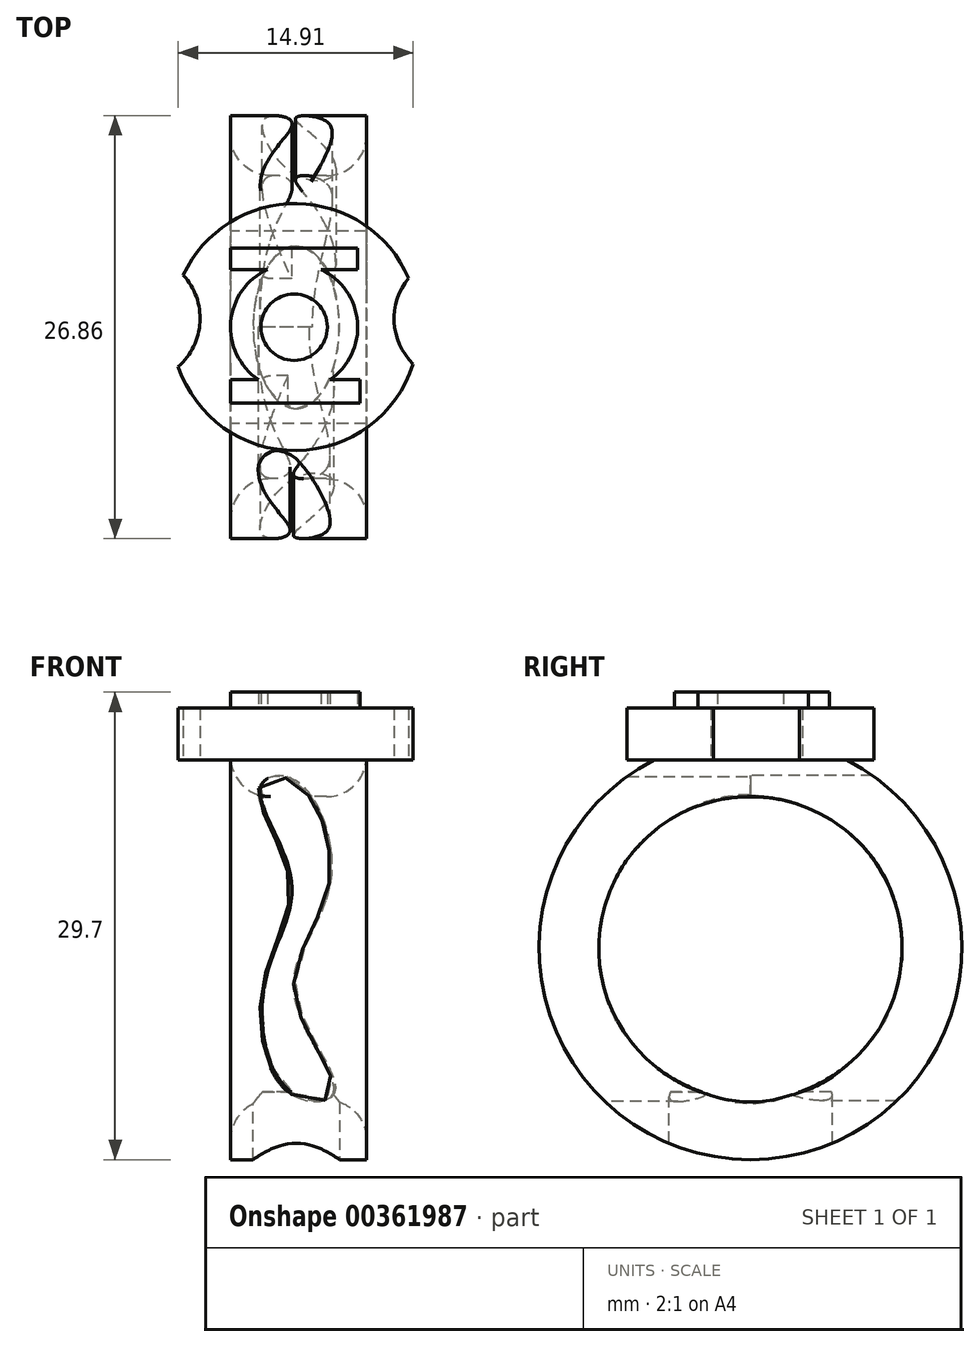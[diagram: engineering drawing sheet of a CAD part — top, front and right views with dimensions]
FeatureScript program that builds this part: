
annotation { "Feature Type Name" : "Feature", "Feature Type Description" : "" }
export const myFeature = defineFeature(function(context is Context, id is Id, definition is map)
    precondition{}
    {
        {
            var Q0;
            Q0=qCreatedBy(makeId("Right.planeOp"),FACE);
            var sketch = newSketch(context, id + "F0", { "sketchPlane" : qUnion([Q0])});
            skCircle(sketch, "E0", {"center": v(0, 9.13) * mm, "radius": 9.63 * mm});
            skCircle(sketch, "E1", {"center": v(0, 9.13) * mm, "radius": 13.43 * mm});
            skArc(sketch, "E2", {"start": v(-4.66, 21.72) * mm, "mid": v(0.04, 18.8) * mm, "end": v(4.75, 21.69) * mm});
            skArc(sketch, "E3", {"start": v(4.75, 21.69) * mm, "mid": v(0.06, 24.06) * mm, "end": v(-4.66, 21.72) * mm});
            skSolve(sketch);
        }
        {
            var Q0;
            Q0 = qSketchRegion(id + "F0", true);
            extrude(context, id + "F1", {"entities" : qUnion([Q0]), "depth" : 8.64 * mm});
        }
        {
            var Q0;
            Q0=makeQuery(id+"F1.opExtrude","CAP_EDGE",EDGE,{"disambiguationData":[OSD([sQuery(id+"F0.wireOp",EDGE,"E0")])],"isStart":false});
            var Q1;
            Q1=makeQuery(id+"F1.opExtrude","CAP_EDGE",EDGE,{"disambiguationData":[OSD([sQuery(id+"F0.wireOp",EDGE,"E0")])],"isStart":true});
            fillet(context, id + "F2", {"entities" : qUnion([Q0, Q1]), "radius" : 2.54 * mm, "tangentPropagation" : true, "allowEdgeOverflow" : false});
        }
        {
            var Q0;
            Q0=qCreatedBy(makeId("Top.planeOp"),FACE);
            cPlane(context, id + "F3", {"entities" : qUnion([Q0]), "cplaneType" : CPlaneType.OFFSET, "offset" : 8.9 * mm, "width" : 152.4 * mm, "height" : 152.4 * mm});
        }
        {
            var Q0;
            Q0=qCreatedBy(makeId("Right.planeOp"),FACE);
            var sketch = newSketch(context, id + "F4", { "sketchPlane" : qUnion([Q0])});
            skCircle(sketch, "E4", {"center": v(11.39, 21.41) * mm, "radius": 5.94 * mm});
            skSolve(sketch);
        }
        {
            var Q0;
            Q0 = qSketchRegion(id + "F4", true);
            extrude(context, id + "F5", {"entities" : qUnion([Q0]), "operationType" : NewBodyOperationType.REMOVE, "depth" : 27.94 * mm});
        }
        {
            var Q0;
            Q0=makeQuery(id+"F1.opExtrude","SWEPT_BODY",BODY,{"disambiguationData":[OSD([sQuery(id+"F0.wireOp",EDGE,"E0"),sQuery(id+"F0.wireOp",EDGE,"E1"),sQuery(id+"F0.wireOp",EDGE,"E3")])]});
            var Q1;
            Q1=qCreatedBy(makeId("Front.planeOp"),FACE);
            mirror(context, id + "F6", {"operationType" : NewBodyOperationType.ADD, "entities" : qUnion([Q0]), "mirrorPlane" : qUnion([Q1])});
        }
        {
            var Q0;
            Q0=qCreatedBy(id+"F3.planeOp",FACE);
            cPlane(context, id + "F7", {"entities" : qUnion([Q0]), "cplaneType" : CPlaneType.OFFSET, "offset" : 12.2 * mm, "width" : 152.4 * mm, "height" : 152.4 * mm});
        }
        {
            var Q0;
            Q0=qCreatedBy(id+"F7.planeOp",FACE);
            var sketch = newSketch(context, id + "F8", { "sketchPlane" : qUnion([Q0])});
            skCircle(sketch, "E5", {"center": v(4.1, 0) * mm, "radius": 7.84 * mm});
            skSolve(sketch);
        }
        {
            var Q0;
            Q0 = qSketchRegion(id + "F8", true);
            extrude(context, id + "F9", {"entities" : qUnion([Q0]), "operationType" : NewBodyOperationType.ADD, "depth" : 3.3 * mm});
        }
        {
            var Q0;
            Q0=qCreatedBy(id+"F7.planeOp",FACE);
            var sketch = newSketch(context, id + "F10", { "sketchPlane" : qUnion([Q0])});
            skLineSegment(sketch, "E6.bottom", {"start": v(0, 5) * mm, "end": v(8.08, 5) * mm});
            skLineSegment(sketch, "E6.top", {"start": v(0, 3.67) * mm, "end": v(8.08, 3.67) * mm});
            skLineSegment(sketch, "E6.left", {"start": v(0, 5) * mm, "end": v(0, 3.67) * mm});
            skLineSegment(sketch, "E6.right", {"start": v(8.08, 5) * mm, "end": v(8.08, 3.67) * mm});
            skLineSegment(sketch, "E7.bottom", {"start": v(0, -3.34) * mm, "end": v(8.23, -3.34) * mm});
            skLineSegment(sketch, "E7.top", {"start": v(0, -4.83) * mm, "end": v(8.23, -4.83) * mm});
            skLineSegment(sketch, "E7.left", {"start": v(0, -3.34) * mm, "end": v(0, -4.83) * mm});
            skLineSegment(sketch, "E7.right", {"start": v(8.23, -3.34) * mm, "end": v(8.23, -4.83) * mm});
            skCircle(sketch, "E8", {"center": v(4.04, 0) * mm, "radius": 4.04 * mm});
            skPoint(sketch, "E8.centerSnap0", {"position": v(4.04, 3.67) * mm});
            skCircle(sketch, "E9", {"center": v(4.04, 0) * mm, "radius": 2.11 * mm});
            skSolve(sketch);
        }
        {
            var Q0;
            Q0 = qSketchRegion(id + "F10", true);
            extrude(context, id + "F11", {"entities" : qUnion([Q0]), "operationType" : NewBodyOperationType.ADD, "depth" : 4.32 * mm});
        }
        {
            var Q0;
            Q0=qCreatedBy(makeId("Front.planeOp"),FACE);
            var sketch = newSketch(context, id + "F12", { "sketchPlane" : qUnion([Q0])});
            skFitSpline(sketch, "E10", {"points": [v(1.92, 19.37) * mm, v(3.86, 13.53) * mm, v(2.2, 7) * mm, v(3.86, 0) * mm, v(6.65, 0) * mm, v(4.15, 6.27) * mm, v(6.38, 13.34) * mm, v(4.02, 19.84) * mm, v(1.92, 19.37) * mm]});
            skSolve(sketch);
        }
        {
            var Q0;
            Q0 = qSketchRegion(id + "F12", true);
            extrude(context, id + "F13", {"entities" : qUnion([Q0]), "operationType" : NewBodyOperationType.REMOVE, "oppositeDirection" : true, "depth" : 45.97 * mm});
        }
        {
            var Q0;
            Q0=qCreatedBy(makeId("Front.planeOp"),FACE);
            var sketch = newSketch(context, id + "F14", { "sketchPlane" : qUnion([Q0])});
            skFitSpline(sketch, "E11", {"points": [v(1.8, 19.32) * mm, v(3.74, 13.47) * mm, v(2.07, 6.94) * mm, v(3.74, -0.06) * mm, v(6.52, -0.06) * mm, v(4.03, 6.21) * mm, v(6.25, 13.28) * mm, v(3.9, 19.79) * mm, v(1.8, 19.32) * mm]});
            skSolve(sketch);
        }
        {
            var Q0;
            Q0 = qSketchRegion(id + "F14", true);
            extrude(context, id + "F15", {"entities" : qUnion([Q0]), "operationType" : NewBodyOperationType.REMOVE, "depth" : 20.32 * mm});
        }
        {
            var Q0;
            Q0=qCreatedBy(makeId("Top.planeOp"),FACE);
            var sketch = newSketch(context, id + "F16", { "sketchPlane" : qUnion([Q0])});
            skArc(sketch, "E12", {"start": v(14.75, 4.56) * mm, "mid": v(10.39, 0.61) * mm, "end": v(14.6, -3.5) * mm});
            skArc(sketch, "E13", {"start": v(14.6, -3.5) * mm, "mid": v(21.27, 0.4) * mm, "end": v(14.75, 4.56) * mm});
            skArc(sketch, "E14", {"start": v(-6.25, -3.5) * mm, "mid": v(-1.94, 0.74) * mm, "end": v(-6.62, 4.56) * mm});
            skArc(sketch, "E15", {"start": v(-6.62, 4.56) * mm, "mid": v(-12.26, 0.26) * mm, "end": v(-6.25, -3.5) * mm});
            skSolve(sketch);
        }
        {
            var Q0;
            Q0 = qSketchRegion(id + "F16", true);
            extrude(context, id + "F17", {"entities" : qUnion([Q0]), "operationType" : NewBodyOperationType.REMOVE, "depth" : 54.86 * mm});
        }
        {
            var Q0;
            Q0=qCreatedBy(makeId("Top.planeOp"),FACE);
            var sketch = newSketch(context, id + "F18", { "sketchPlane" : qUnion([Q0])});
            skEllipse(sketch, "E16", {"center": v(4.17, 0) * mm, "majorRadius": 5.17 * mm, "minorRadius": 2.74 * mm, "majorAxis": v(0, -1)});
            skSolve(sketch);
        }
        {
            var Q0;
            Q0 = qSketchRegion(id + "F18", true);
            extrude(context, id + "F19", {"entities" : qUnion([Q0]), "operationType" : NewBodyOperationType.REMOVE, "oppositeDirection" : true, "depth" : 19.05 * mm});
        }
    });
